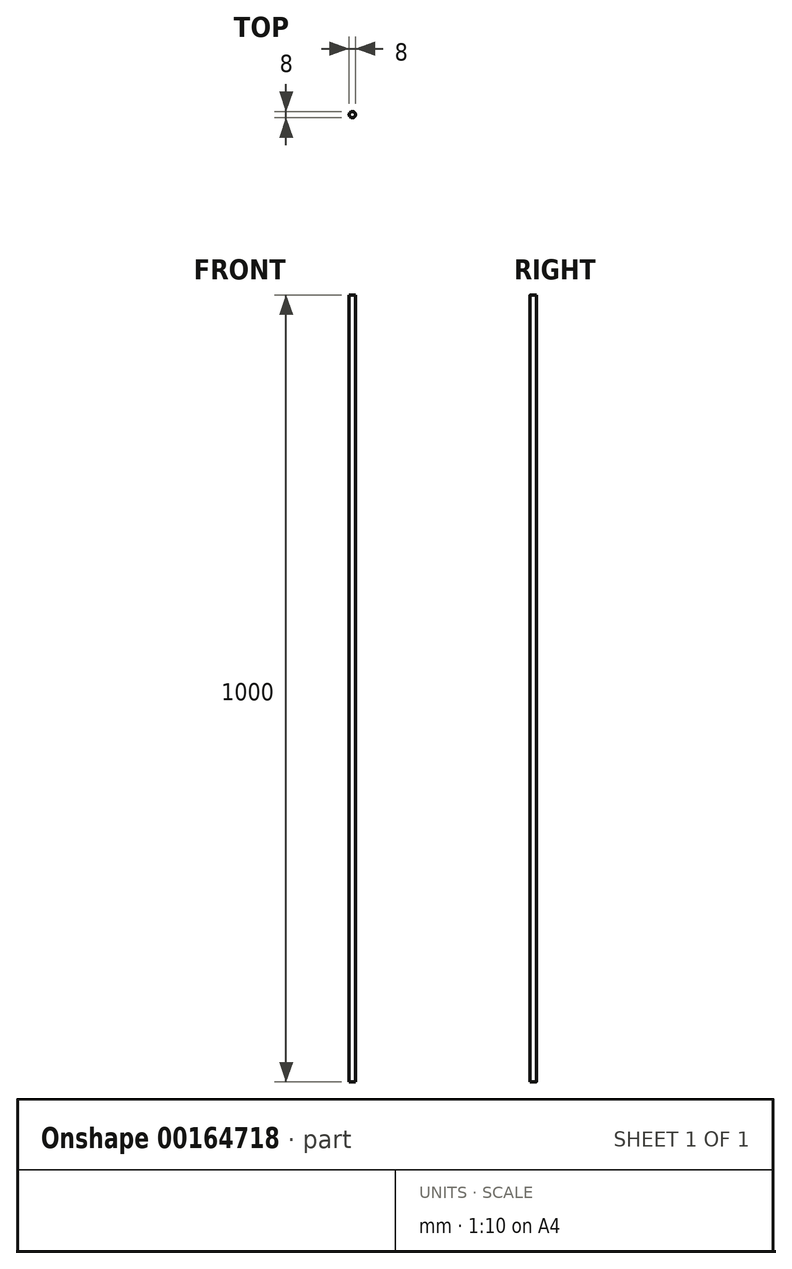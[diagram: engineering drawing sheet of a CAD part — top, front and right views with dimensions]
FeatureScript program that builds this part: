
annotation { "Feature Type Name" : "Feature", "Feature Type Description" : "" }
export const myFeature = defineFeature(function(context is Context, id is Id, definition is map)
    precondition{}
    {
        {
            var Q0;
            Q0=qCreatedBy(makeId("Top.planeOp"),FACE);
            var sketch = newSketch(context, id + "F0", { "sketchPlane" : qUnion([Q0])});
            skCircle(sketch, "E0", {"center": v(0, 0) * mm, "radius": 4 * mm});
            skSolve(sketch);
        }
        {
            var Q0;
            Q0=makeQuery(id+"F0.imprint","IMPRINT",FACE,{"disambiguationData":[TD([[makeQuery(id+"F0.imprint","IMPRINT",EDGE,{"derivedFrom":sQuery(id+"F0.wireOp",EDGE,"E0")}),1.0]])]});
            extrude(context, id + "F1", {"entities" : qUnion([Q0]), "depth" : 1000 * mm});
        }
    });
